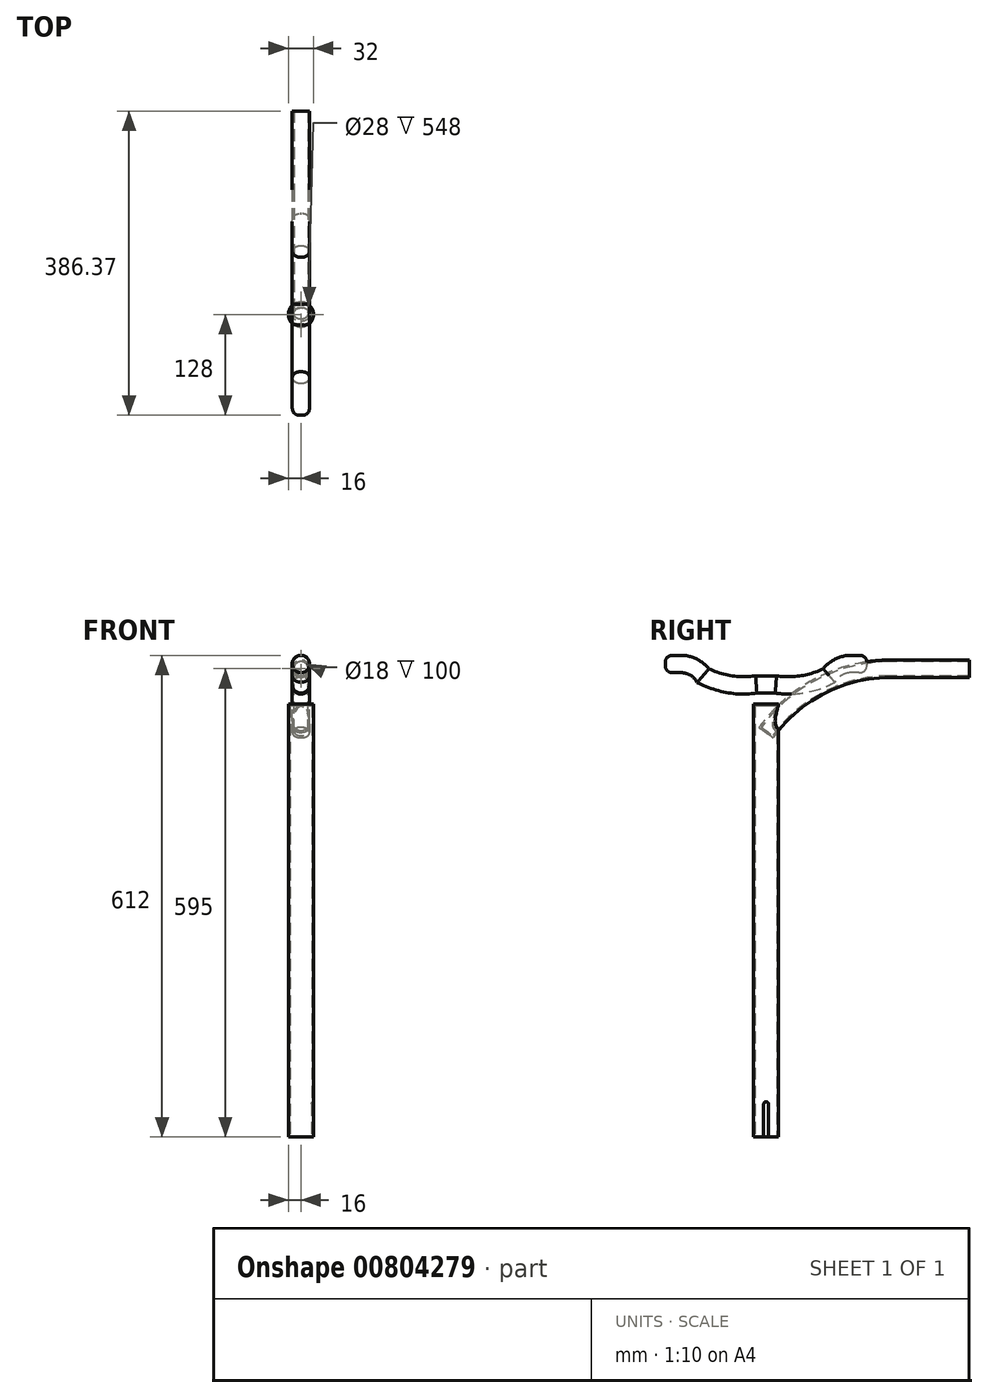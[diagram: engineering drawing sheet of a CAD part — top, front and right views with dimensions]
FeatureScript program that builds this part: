
annotation { "Feature Type Name" : "Feature", "Feature Type Description" : "" }
export const myFeature = defineFeature(function(context is Context, id is Id, definition is map)
    precondition{}
    {
        {
            var Q0;
            Q0=qCreatedBy(makeId("Top.planeOp"),FACE);
            var sketch = newSketch(context, id + "F0", { "sketchPlane" : qUnion([Q0])});
            skCircle(sketch, "E0", {"center": v(0, 0) * mm, "radius": 16 * mm});
            skSolve(sketch);
        }
        {
            var Q0;
            Q0 = qSketchRegion(id + "F0", true);
            var Q1;
            Q1=makeQuery(id+"F0.imprint","IMPRINT",FACE,{"disambiguationData":[TD([[makeQuery(id+"F0.imprint","IMPRINT",EDGE,{"derivedFrom":sQuery(id+"F0.wireOp",EDGE,"E0")}),1.0]])]});
            extrude(context, id + "F1", {"entities" : qUnion([Q0, Q1]), "depth" : 550 * mm, "offsetDistance" : 25 * mm});
        }
        {
            var Q0;
            Q0=makeQuery(id+"F1.opExtrude","CAP_FACE",FACE,{"disambiguationData":[OSD([sQuery(id+"F0.wireOp",EDGE,"E0")])],"isStart":true});
            shell(context, id + "F2", {"entities" : qUnion([Q0]), "thickness" : 2 * mm});
        }
        {
            var Q0;
            Q0=qCreatedBy(makeId("Right.planeOp"),FACE);
            var sketch = newSketch(context, id + "F3", { "sketchPlane" : qUnion([Q0])});
            skLineSegment(sketch, "E1.bottom", {"start": v(3, 0) * mm, "end": v(-3, 0) * mm});
            skLineSegment(sketch, "E1.top", {"start": v(0, 45) * mm, "end": v(0, 45) * mm});
            skLineSegment(sketch, "E1.left", {"start": v(3, 0) * mm, "end": v(3, 42) * mm});
            skLineSegment(sketch, "E1.right", {"start": v(-3, 0) * mm, "end": v(-3, 42) * mm});
            skPoint(sketch, "E2.visualSharp", {"position": v(-3, 45) * mm});
            skArc(sketch, "E2.filletArc", {"start": v(0, 45) * mm, "mid": v(-2.12, 44.12) * mm, "end": v(-3, 42) * mm});
            skPoint(sketch, "E3.visualSharp", {"position": v(3, 45) * mm});
            skArc(sketch, "E3.filletArc", {"start": v(3, 42) * mm, "mid": v(2.12, 44.12) * mm, "end": v(0, 45) * mm});
            skSolve(sketch);
        }
        {
            var Q0;
            Q0 = qSketchRegion(id + "F3", true);
            extrude(context, id + "F4", {"entities" : qUnion([Q0]), "operationType" : NewBodyOperationType.REMOVE, "endBound" : BoundingType.THROUGH_ALL, "depth" : 25 * mm, "offsetDistance" : 25 * mm});
        }
        {
            var Q0;
            Q0=qCreatedBy(makeId("Right.planeOp"),FACE);
            var sketch = newSketch(context, id + "F5", { "sketchPlane" : qUnion([Q0])});
            skArc(sketch, "E4", {"start": v(158.37, 595) * mm, "mid": v(69.38, 573.5) * mm, "end": v(0, 513.77) * mm});
            skLineSegment(sketch, "E5", {"start": v(158.37, 595) * mm, "end": v(258.37, 595) * mm});
            skSolve(sketch);
        }
        {
            var Q0;
            Q0=sQuery(id+"F5.wireOp",VERTEX,"E5.end");
            var Q1;
            Q1=qCreatedBy(makeId("Front.planeOp"),FACE);
            cPlane(context, id + "F6", {"entities" : qUnion([Q0, Q1]), "cplaneType" : CPlaneType.PLANE_POINT, "offset" : 25 * mm, "width" : 150 * mm, "height" : 150 * mm});
        }
        {
            var Q0;
            Q0=qCreatedBy(id+"F6.planeOp",FACE);
            var sketch = newSketch(context, id + "F7", { "sketchPlane" : qUnion([Q0])});
            skCircle(sketch, "E6", {"center": v(0, 595) * mm, "radius": 11 * mm});
            skSolve(sketch);
        }
        {
            var Q0;
            Q0=makeQuery(id+"F7.imprint","IMPRINT",FACE,{"disambiguationData":[TD([[makeQuery(id+"F7.imprint","IMPRINT",EDGE,{"derivedFrom":sQuery(id+"F7.wireOp",EDGE,"E6")}),1.0]])]});
            var Q1;
            Q1=sQuery(id+"F5.wireOp",EDGE,"E4");
            var Q2;
            Q2=sQuery(id+"F5.wireOp",EDGE,"E5");
            sweep(context, id + "F8", {"operationType" : NewBodyOperationType.ADD, "profiles" : qUnion([Q0]), "path" : qUnion([Q1, Q2])});
        }
        {
            var Q0;
            Q0=makeQuery(id+"F8.opSweep","CAP_FACE",FACE,{"disambiguationData":[OSD([sQuery(id+"F5.wireOp",VERTEX,"E5.end"),sQuery(id+"F7.wireOp",EDGE,"E6")])],"isStart":true});
            shell(context, id + "F9", {"entities" : qUnion([Q0]), "thickness" : 2 * mm});
        }
        {
            var Q0;
            Q0=qCreatedBy(makeId("Right.planeOp"),FACE);
            var sketch = newSketch(context, id + "F10", { "sketchPlane" : qUnion([Q0])});
            skLineSegment(sketch, "E7", {"start": v(0, 535.43) * mm, "end": v(0, 616.7) * mm, "construction": true});
            skLineSegment(sketch, "E8", {"start": v(-128, 601) * mm, "end": v(-108, 601) * mm});
            skArc(sketch, "E9", {"start": v(-79.96, 586.23) * mm, "mid": v(-92.16, 597.08) * mm, "end": v(-108, 601) * mm});
            skArc(sketch, "E10", {"start": v(-79.96, 586.23) * mm, "mid": v(-47.11, 575.34) * mm, "end": v(-12.5, 575) * mm});
            skLineSegment(sketch, "E11", {"start": v(-12.5, 575) * mm, "end": v(0, 575) * mm});
            skArc(sketch, "E12.MirrorCS", {"start": v(79.96, 586.23) * mm, "mid": v(47.11, 575.34) * mm, "end": v(12.5, 575) * mm});
            skArc(sketch, "E13.MirrorCS", {"start": v(79.96, 586.23) * mm, "mid": v(92.16, 597.08) * mm, "end": v(108, 601) * mm});
            skLineSegment(sketch, "E14.MirrorCS", {"start": v(128, 601) * mm, "end": v(108, 601) * mm});
            skLineSegment(sketch, "E15.MirrorCS", {"start": v(12.5, 575) * mm, "end": v(0, 575) * mm});
            skSolve(sketch);
        }
        {
            var Q0;
            Q0=sQuery(id+"F10.wireOp",VERTEX,"E14.MirrorCS.start");
            var Q1;
            Q1=qCreatedBy(id+"F6.planeOp",FACE);
            cPlane(context, id + "F11", {"entities" : qUnion([Q0, Q1]), "cplaneType" : CPlaneType.PLANE_POINT, "offset" : 25 * mm, "width" : 150 * mm, "height" : 150 * mm});
        }
        {
            var Q0;
            Q0=qCreatedBy(id+"F11.planeOp",FACE);
            var sketch = newSketch(context, id + "F12", { "sketchPlane" : qUnion([Q0])});
            skCircle(sketch, "E16", {"center": v(0, 601) * mm, "radius": 11 * mm});
            skSolve(sketch);
        }
        {
            var Q0;
            Q0=makeQuery(id+"F12.imprint","IMPRINT",FACE,{"disambiguationData":[TD([[makeQuery(id+"F12.imprint","IMPRINT",EDGE,{"derivedFrom":sQuery(id+"F12.wireOp",EDGE,"E16")}),1.0]])]});
            var Q1;
            Q1 = qConstructionFilter(qBodyType(qCreatedBy(id + "F10" ,EDGE), BodyType.WIRE), ConstructionObject.NO);
            sweep(context, id + "F13", {"profiles" : qUnion([Q0]), "path" : qUnion([Q1])});
        }
        {
            var Q0;
            Q0=makeQuery(id+"F13.opSweep","CAP_EDGE",EDGE,{"disambiguationData":[OSD([sQuery(id+"F10.wireOp",VERTEX,"E14.MirrorCS.start"),sQuery(id+"F12.wireOp",EDGE,"E16")])],"isStart":true});
            var Q1;
            Q1=makeQuery(id+"F13.opSweep","CAP_EDGE",EDGE,{"disambiguationData":[OSD([sQuery(id+"F10.wireOp",VERTEX,"E8.start"),sQuery(id+"F12.wireOp",EDGE,"E16")])],"isStart":false});
            fillet(context, id + "F14", {"entities" : qUnion([Q0, Q1]), "radius" : 10 * mm, "tangentPropagation" : true, "rho" : 0.5, "crossSection" : FilletCrossSection.CONIC, "allowEdgeOverflow" : false});
        }
    });
